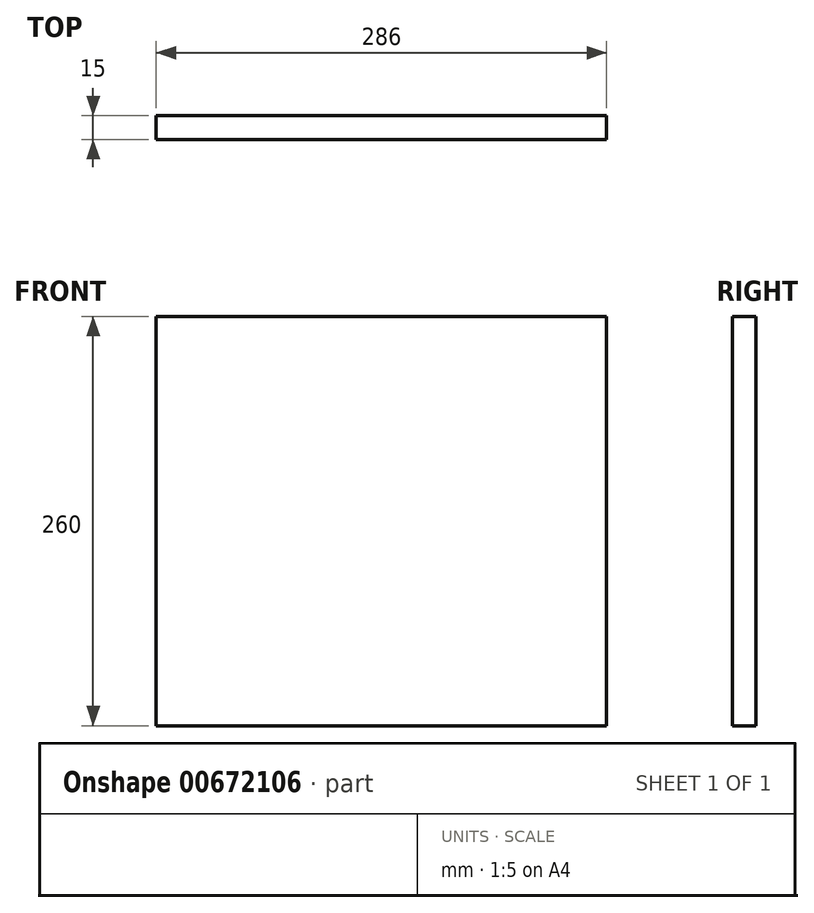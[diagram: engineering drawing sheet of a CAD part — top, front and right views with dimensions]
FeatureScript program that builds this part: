
annotation { "Feature Type Name" : "Feature", "Feature Type Description" : "" }
export const myFeature = defineFeature(function(context is Context, id is Id, definition is map)
    precondition{}
    {
        {
            var Q0;
            Q0=qCreatedBy(makeId("Front.planeOp"),FACE);
            var sketch = newSketch(context, id + "F0", { "sketchPlane" : qUnion([Q0])});
            skLineSegment(sketch, "E0.bottom", {"start": v(-138.48, 175.37) * mm, "end": v(147.52, 175.37) * mm});
            skLineSegment(sketch, "E0.top", {"start": v(-138.48, -84.63) * mm, "end": v(147.52, -84.63) * mm});
            skLineSegment(sketch, "E0.left", {"start": v(-138.48, 175.37) * mm, "end": v(-138.48, -84.63) * mm});
            skLineSegment(sketch, "E0.right", {"start": v(147.52, 175.37) * mm, "end": v(147.52, -84.63) * mm});
            skSolve(sketch);
        }
        {
            var Q0;
            Q0 = qSketchRegion(id + "F0", true);
            extrude(context, id + "F1", {"entities" : qUnion([Q0]), "oppositeDirection" : true, "depth" : 15 * mm, "offsetDistance" : 25 * mm});
        }
    });
